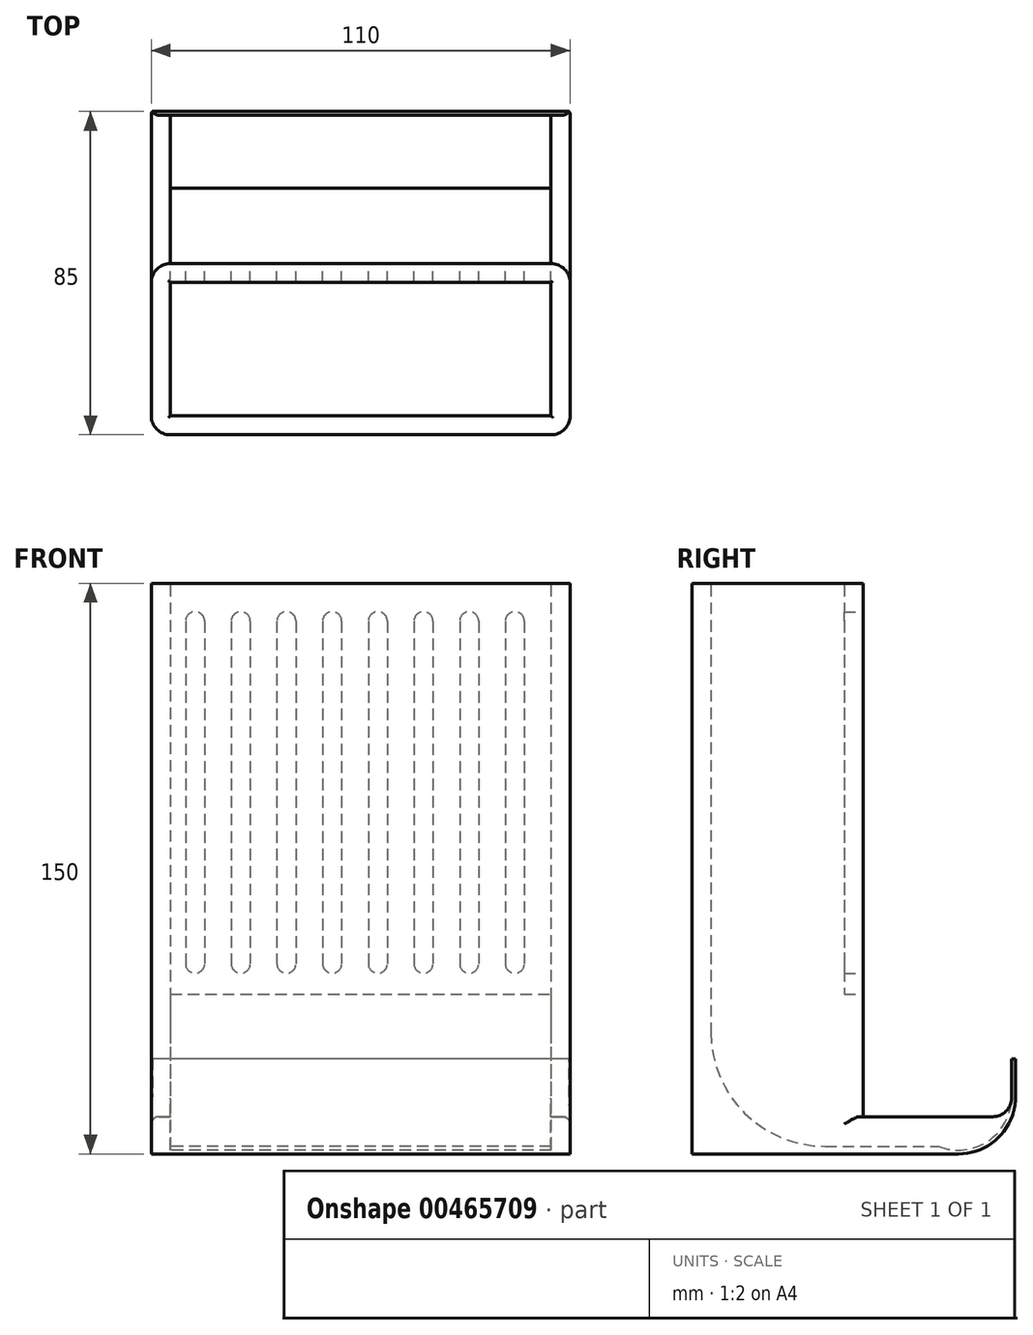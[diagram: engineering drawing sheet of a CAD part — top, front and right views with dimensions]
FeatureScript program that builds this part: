
annotation { "Feature Type Name" : "Feature", "Feature Type Description" : "" }
export const myFeature = defineFeature(function(context is Context, id is Id, definition is map)
    precondition{}
    {
        {
            var Q0;
            Q0=qCreatedBy(makeId("Right.planeOp"),FACE);
            var sketch = newSketch(context, id + "F0", { "sketchPlane" : qUnion([Q0])});
            skLineSegment(sketch, "E0.bottom", {"start": v(0, 150) * mm, "end": v(45, 150) * mm});
            skLineSegment(sketch, "E0.top", {"start": v(0, 0) * mm, "end": v(45, 0) * mm});
            skLineSegment(sketch, "E0.left", {"start": v(0, 150) * mm, "end": v(0, 0) * mm});
            skLineSegment(sketch, "E0.right", {"start": v(45, 150) * mm, "end": v(45, 32) * mm});
            skLineSegment(sketch, "E1.bottom", {"start": v(0, 0) * mm, "end": v(70, 0) * mm});
            skLineSegment(sketch, "E1.left", {"start": v(0, 0) * mm, "end": v(0, 32) * mm});
            skLineSegment(sketch, "E1.right", {"start": v(85, 15) * mm, "end": v(85, 25) * mm});
            skArc(sketch, "E2", {"start": v(70, 0) * mm, "mid": v(80.6, 4.4) * mm, "end": v(85, 15) * mm});
            skLineSegment(sketch, "E3", {"start": v(45, 32) * mm, "end": v(45, 9.79) * mm});
            skLineSegment(sketch, "E4.bottom", {"start": v(45, 9.79) * mm, "end": v(83, 9.79) * mm});
            skLineSegment(sketch, "E4.top", {"start": v(32, 0) * mm, "end": v(70, 0) * mm});
            skPoint(sketch, "E5.orphan", {"position": v(65.24, 0) * mm});
            skArc(sketch, "E6", {"start": v(83, 9.79) * mm, "mid": v(83.75, 12.35) * mm, "end": v(84, 15) * mm});
            skLineSegment(sketch, "E7", {"start": v(84, 15) * mm, "end": v(84, 25) * mm});
            skLineSegment(sketch, "E8", {"start": v(85, 25) * mm, "end": v(84, 25) * mm});
            skSolve(sketch);
        }
        {
            var Q0;
            Q0 = qSketchRegion(id + "F0", true);
            extrude(context, id + "F1", {"entities" : qUnion([Q0]), "depth" : 110 * mm});
        }
        {
            var Q0;
            Q0=qCreatedBy(makeId("Right.planeOp"),FACE);
            cPlane(context, id + "F2", {"entities" : qUnion([Q0]), "cplaneType" : CPlaneType.OFFSET, "offset" : 55 * mm, "width" : 150 * mm, "height" : 150 * mm});
        }
        {
            var Q0;
            Q0=qCreatedBy(id+"F2.planeOp",FACE);
            var sketch = newSketch(context, id + "F3", { "sketchPlane" : qUnion([Q0])});
            skArc(sketch, "E9", {"start": v(64.8, 2) * mm, "mid": v(81.9, 7.6) * mm, "end": v(79.36, 25.41) * mm});
            skLineSegment(sketch, "E10.bottom", {"start": v(5, 152) * mm, "end": v(40, 152) * mm});
            skLineSegment(sketch, "E10.top", {"start": v(5, 2) * mm, "end": v(40, 2) * mm});
            skLineSegment(sketch, "E10.left", {"start": v(5, 152) * mm, "end": v(5, 2) * mm});
            skLineSegment(sketch, "E10.right", {"start": v(40, 152) * mm, "end": v(40, 42) * mm});
            skLineSegment(sketch, "E11.top", {"start": v(26.38, 2) * mm, "end": v(45.83, 2) * mm});
            skPoint(sketch, "E12.start.orphan", {"position": v(54.41, 2) * mm});
            skLineSegment(sketch, "E13", {"start": v(35.85, 2) * mm, "end": v(64.8, 2) * mm});
            skLineSegment(sketch, "E14", {"start": v(40, 42) * mm, "end": v(79.36, 42) * mm});
            skLineSegment(sketch, "E15", {"start": v(79.36, 25.41) * mm, "end": v(79.36, 42) * mm});
            skSolve(sketch);
        }
        {
            var Q0;
            Q0 = qSketchRegion(id + "F3", true);
            extrude(context, id + "F4", {"entities" : qUnion([Q0]), "operationType" : NewBodyOperationType.REMOVE, "endBound" : BoundingType.SYMMETRIC, "depth" : 100 * mm});
        }
        {
            var Q0;
            Q0=makeQuery(id+"F1.opExtrude","SWEPT_FACE",FACE,{"disambiguationData":[OSD([sQuery(id+"F0.wireOp",EDGE,"E0.right"),sQuery(id+"F0.wireOp",EDGE,"E3")])]});
            var sketch = newSketch(context, id + "F5", { "sketchPlane" : qUnion([Q0])});
            skLineSegment(sketch, "E16.left", {"start": v(-98, 140) * mm, "end": v(-98, 50) * mm});
            skLineSegment(sketch, "E16.right", {"start": v(-93, 140) * mm, "end": v(-93, 50) * mm});
            skArc(sketch, "E17", {"start": v(-93, 140) * mm, "mid": v(-95.5, 142.5) * mm, "end": v(-98, 140) * mm});
            skArc(sketch, "E18", {"start": v(-98, 50) * mm, "mid": v(-95.5, 47.5) * mm, "end": v(-93, 50) * mm});
            skArc(sketch, "E19.1.0.0", {"start": v(-81, 140) * mm, "mid": v(-83.5, 142.5) * mm, "end": v(-86, 140) * mm});
            skLineSegment(sketch, "E19.1.0.1", {"start": v(-86, 140) * mm, "end": v(-86, 50) * mm});
            skLineSegment(sketch, "E19.1.0.2", {"start": v(-81, 140) * mm, "end": v(-81, 50) * mm});
            skArc(sketch, "E19.1.0.3", {"start": v(-86, 50) * mm, "mid": v(-83.5, 47.5) * mm, "end": v(-81, 50) * mm});
            skArc(sketch, "E19.2.0.0", {"start": v(-69, 140) * mm, "mid": v(-71.5, 142.5) * mm, "end": v(-74, 140) * mm});
            skLineSegment(sketch, "E19.2.0.1", {"start": v(-74, 140) * mm, "end": v(-74, 50) * mm});
            skLineSegment(sketch, "E19.2.0.2", {"start": v(-69, 140) * mm, "end": v(-69, 50) * mm});
            skArc(sketch, "E19.2.0.3", {"start": v(-74, 50) * mm, "mid": v(-71.5, 47.5) * mm, "end": v(-69, 50) * mm});
            skArc(sketch, "E19.3.0.0", {"start": v(-57, 140) * mm, "mid": v(-59.5, 142.5) * mm, "end": v(-62, 140) * mm});
            skLineSegment(sketch, "E19.3.0.1", {"start": v(-62, 140) * mm, "end": v(-62, 50) * mm});
            skLineSegment(sketch, "E19.3.0.2", {"start": v(-57, 140) * mm, "end": v(-57, 50) * mm});
            skArc(sketch, "E19.3.0.3", {"start": v(-62, 50) * mm, "mid": v(-59.5, 47.5) * mm, "end": v(-57, 50) * mm});
            skArc(sketch, "E19.4.0.0", {"start": v(-45, 140) * mm, "mid": v(-47.5, 142.5) * mm, "end": v(-50, 140) * mm});
            skLineSegment(sketch, "E19.4.0.1", {"start": v(-50, 140) * mm, "end": v(-50, 50) * mm});
            skLineSegment(sketch, "E19.4.0.2", {"start": v(-45, 140) * mm, "end": v(-45, 50) * mm});
            skArc(sketch, "E19.4.0.3", {"start": v(-50, 50) * mm, "mid": v(-47.5, 47.5) * mm, "end": v(-45, 50) * mm});
            skArc(sketch, "E19.5.0.0", {"start": v(-33, 140) * mm, "mid": v(-35.5, 142.5) * mm, "end": v(-38, 140) * mm});
            skLineSegment(sketch, "E19.5.0.1", {"start": v(-38, 140) * mm, "end": v(-38, 50) * mm});
            skLineSegment(sketch, "E19.5.0.2", {"start": v(-33, 140) * mm, "end": v(-33, 50) * mm});
            skArc(sketch, "E19.5.0.3", {"start": v(-38, 50) * mm, "mid": v(-35.5, 47.5) * mm, "end": v(-33, 50) * mm});
            skLineSegment(sketch, "E19.direction1", {"start": v(-98, 140) * mm, "end": v(-86, 140) * mm, "construction": true});
            skArc(sketch, "E20.0.6.0", {"start": v(-21, 140) * mm, "mid": v(-23.5, 142.5) * mm, "end": v(-26, 140) * mm});
            skLineSegment(sketch, "E20.4.6.0", {"start": v(-26, 140) * mm, "end": v(-26, 50) * mm});
            skLineSegment(sketch, "E20.7.6.0", {"start": v(-21, 140) * mm, "end": v(-21, 50) * mm});
            skArc(sketch, "E20.10.6.0", {"start": v(-26, 50) * mm, "mid": v(-23.5, 47.5) * mm, "end": v(-21, 50) * mm});
            skArc(sketch, "E21.0.7.0", {"start": v(-9, 140) * mm, "mid": v(-11.5, 142.5) * mm, "end": v(-14, 140) * mm});
            skLineSegment(sketch, "E21.4.7.0", {"start": v(-14, 140) * mm, "end": v(-14, 50) * mm});
            skLineSegment(sketch, "E21.7.7.0", {"start": v(-9, 140) * mm, "end": v(-9, 50) * mm});
            skArc(sketch, "E21.10.7.0", {"start": v(-14, 50) * mm, "mid": v(-11.5, 47.5) * mm, "end": v(-9, 50) * mm});
            skSolve(sketch);
        }
        {
            var Q0;
            Q0 = qSketchRegion(id + "F5", true);
            extrude(context, id + "F6", {"entities" : qUnion([Q0]), "operationType" : NewBodyOperationType.REMOVE, "oppositeDirection" : true, "depth" : 5 * mm});
        }
        {
            var Q0;
            Q0=makeQuery(id+"F1.opExtrude","CAP_EDGE",EDGE,{"disambiguationData":[OSD([sQuery(id+"F0.wireOp",EDGE,"E0.left"),sQuery(id+"F0.wireOp",EDGE,"E1.left")])],"isStart":true});
            var Q1;
            Q1=makeQuery(id+"F1.opExtrude","CAP_EDGE",EDGE,{"disambiguationData":[OSD([sQuery(id+"F0.wireOp",EDGE,"E0.left"),sQuery(id+"F0.wireOp",EDGE,"E1.left")])],"isStart":false});
            var Q2;
            Q2=makeQuery(id+"F1.opExtrude","CAP_EDGE",EDGE,{"disambiguationData":[OSD([sQuery(id+"F0.wireOp",EDGE,"E0.right"),sQuery(id+"F0.wireOp",EDGE,"E3")])],"isStart":false});
            var Q3;
            Q3=makeQuery(id+"F1.opExtrude","CAP_EDGE",EDGE,{"disambiguationData":[OSD([sQuery(id+"F0.wireOp",EDGE,"E0.right"),sQuery(id+"F0.wireOp",EDGE,"E3")])],"isStart":true});
            fillet(context, id + "F7", {"entities" : qUnion([Q0, Q1, Q2, Q3]), "radius" : 5 * mm, "tangentPropagation" : true, "allowEdgeOverflow" : false});
        }
        {
            var Q0;
            {var subQ0=sQuery(id+"F3.wireOp",EDGE,"E9");var subQ1=sQuery(id+"F0.wireOp",EDGE,"E6");var subQ2=sQuery(id+"F0.wireOp",EDGE,"E4.bottom");Q0=makeQuery(id+"F4.boolean.opBoolean","SPLIT",EDGE,{"disambiguationData":[TD([makeQuery(id+"F4.opExtrude","CAP_FACE",FACE,{"disambiguationData":[OSD([subQ0,sQuery(id+"F3.wireOp",EDGE,"E10.bottom"),sQuery(id+"F3.wireOp",EDGE,"E10.top"),sQuery(id+"F3.wireOp",EDGE,"E10.left"),sQuery(id+"F3.wireOp",EDGE,"E10.right"),sQuery(id+"F3.wireOp",EDGE,"E11.bottom"),sQuery(id+"F3.wireOp",EDGE,"E11.top")])],"isStart":false})])],"derivedFrom":makeQuery(id+"F1.opExtrude","SWEPT_EDGE",EDGE,{"disambiguationData":[OSD([subQ2,subQ1])]})});}
            var Q1;
            {var subQ0=sQuery(id+"F3.wireOp",EDGE,"E9");var subQ1=sQuery(id+"F0.wireOp",EDGE,"E6");var subQ2=sQuery(id+"F0.wireOp",EDGE,"E4.bottom");Q1=makeQuery(id+"F4.boolean.opBoolean","SPLIT",EDGE,{"disambiguationData":[TD([makeQuery(id+"F4.opExtrude","CAP_FACE",FACE,{"disambiguationData":[OSD([subQ0,sQuery(id+"F3.wireOp",EDGE,"E10.bottom"),sQuery(id+"F3.wireOp",EDGE,"E10.top"),sQuery(id+"F3.wireOp",EDGE,"E10.left"),sQuery(id+"F3.wireOp",EDGE,"E10.right"),sQuery(id+"F3.wireOp",EDGE,"E11.bottom"),sQuery(id+"F3.wireOp",EDGE,"E11.top")])],"isStart":true})])],"derivedFrom":makeQuery(id+"F1.opExtrude","SWEPT_EDGE",EDGE,{"disambiguationData":[OSD([subQ2,subQ1])]})});}
            fillet(context, id + "F8", {"entities" : qUnion([Q0, Q1]), "radius" : 5 * mm, "tangentPropagation" : true, "allowEdgeOverflow" : false});
        }
        {
            var Q0;
            Q0=makeQuery(id+"F4.boolean.opBoolean","INTERSECT",EDGE,{"derivedFrom":[makeQuery(id+"F1.opExtrude","SWEPT_FACE",FACE,{"disambiguationData":[OSD([sQuery(id+"F0.wireOp",EDGE,"E0.bottom")])]}),makeQuery(id+"F4.opExtrude","SWEPT_FACE",FACE,{"disambiguationData":[OSD([sQuery(id+"F3.wireOp",EDGE,"E10.left")])]})]});
            var Q1;
            Q1=makeQuery(id+"F4.boolean.opBoolean","INTERSECT",EDGE,{"derivedFrom":[makeQuery(id+"F1.opExtrude","SWEPT_FACE",FACE,{"disambiguationData":[OSD([sQuery(id+"F0.wireOp",EDGE,"E0.bottom")])]}),makeQuery(id+"F4.opExtrude","CAP_FACE",FACE,{"disambiguationData":[OSD([sQuery(id+"F3.wireOp",EDGE,"E9"),sQuery(id+"F3.wireOp",EDGE,"E10.bottom"),sQuery(id+"F3.wireOp",EDGE,"E10.top"),sQuery(id+"F3.wireOp",EDGE,"E10.left"),sQuery(id+"F3.wireOp",EDGE,"E10.right"),sQuery(id+"F3.wireOp",EDGE,"E11.bottom"),sQuery(id+"F3.wireOp",EDGE,"E11.top")])],"isStart":true})]});
            var Q2;
            Q2=makeQuery(id+"F4.boolean.opBoolean","INTERSECT",EDGE,{"derivedFrom":[makeQuery(id+"F1.opExtrude","SWEPT_FACE",FACE,{"disambiguationData":[OSD([sQuery(id+"F0.wireOp",EDGE,"E0.bottom")])]}),makeQuery(id+"F4.opExtrude","SWEPT_FACE",FACE,{"disambiguationData":[OSD([sQuery(id+"F3.wireOp",EDGE,"E10.right")])]})]});
            var Q3;
            Q3=makeQuery(id+"F4.boolean.opBoolean","INTERSECT",EDGE,{"derivedFrom":[makeQuery(id+"F1.opExtrude","SWEPT_FACE",FACE,{"disambiguationData":[OSD([sQuery(id+"F0.wireOp",EDGE,"E0.bottom")])]}),makeQuery(id+"F4.opExtrude","CAP_FACE",FACE,{"disambiguationData":[OSD([sQuery(id+"F3.wireOp",EDGE,"E9"),sQuery(id+"F3.wireOp",EDGE,"E10.bottom"),sQuery(id+"F3.wireOp",EDGE,"E10.top"),sQuery(id+"F3.wireOp",EDGE,"E10.left"),sQuery(id+"F3.wireOp",EDGE,"E10.right"),sQuery(id+"F3.wireOp",EDGE,"E11.bottom"),sQuery(id+"F3.wireOp",EDGE,"E11.top")])],"isStart":false})]});
            fillet(context, id + "F9", {"entities" : qUnion([Q0, Q1, Q2, Q3]), "radius" : .5 * mm, "tangentPropagation" : true, "allowEdgeOverflow" : false});
        }
        {
            var Q0;
            Q0=makeQuery(id+"F1.opExtrude","CAP_EDGE",EDGE,{"disambiguationData":[OSD([sQuery(id+"F0.wireOp",EDGE,"E4.bottom")])],"isStart":false});
            var Q1;
            Q1=makeQuery(id+"F1.opExtrude","CAP_EDGE",EDGE,{"disambiguationData":[OSD([sQuery(id+"F0.wireOp",EDGE,"E4.bottom")])],"isStart":true});
            fillet(context, id + "F10", {"entities" : qUnion([Q0, Q1]), "radius" : 2 * mm, "tangentPropagation" : true, "allowEdgeOverflow" : false});
        }
        {
            var Q0;
            Q0=makeQuery(id+"F4.boolean.opBoolean","COPY",EDGE,{"derivedFrom":makeQuery(id+"F4.opExtrude","SWEPT_EDGE",EDGE,{"disambiguationData":[OSD([sQuery(id+"F3.wireOp",EDGE,"E10.top"),sQuery(id+"F3.wireOp",EDGE,"E10.left")])]})});
            fillet(context, id + "F11", {"entities" : qUnion([Q0]), "radius" : 30 * mm, "tangentPropagation" : true, "allowEdgeOverflow" : false});
        }
    });
